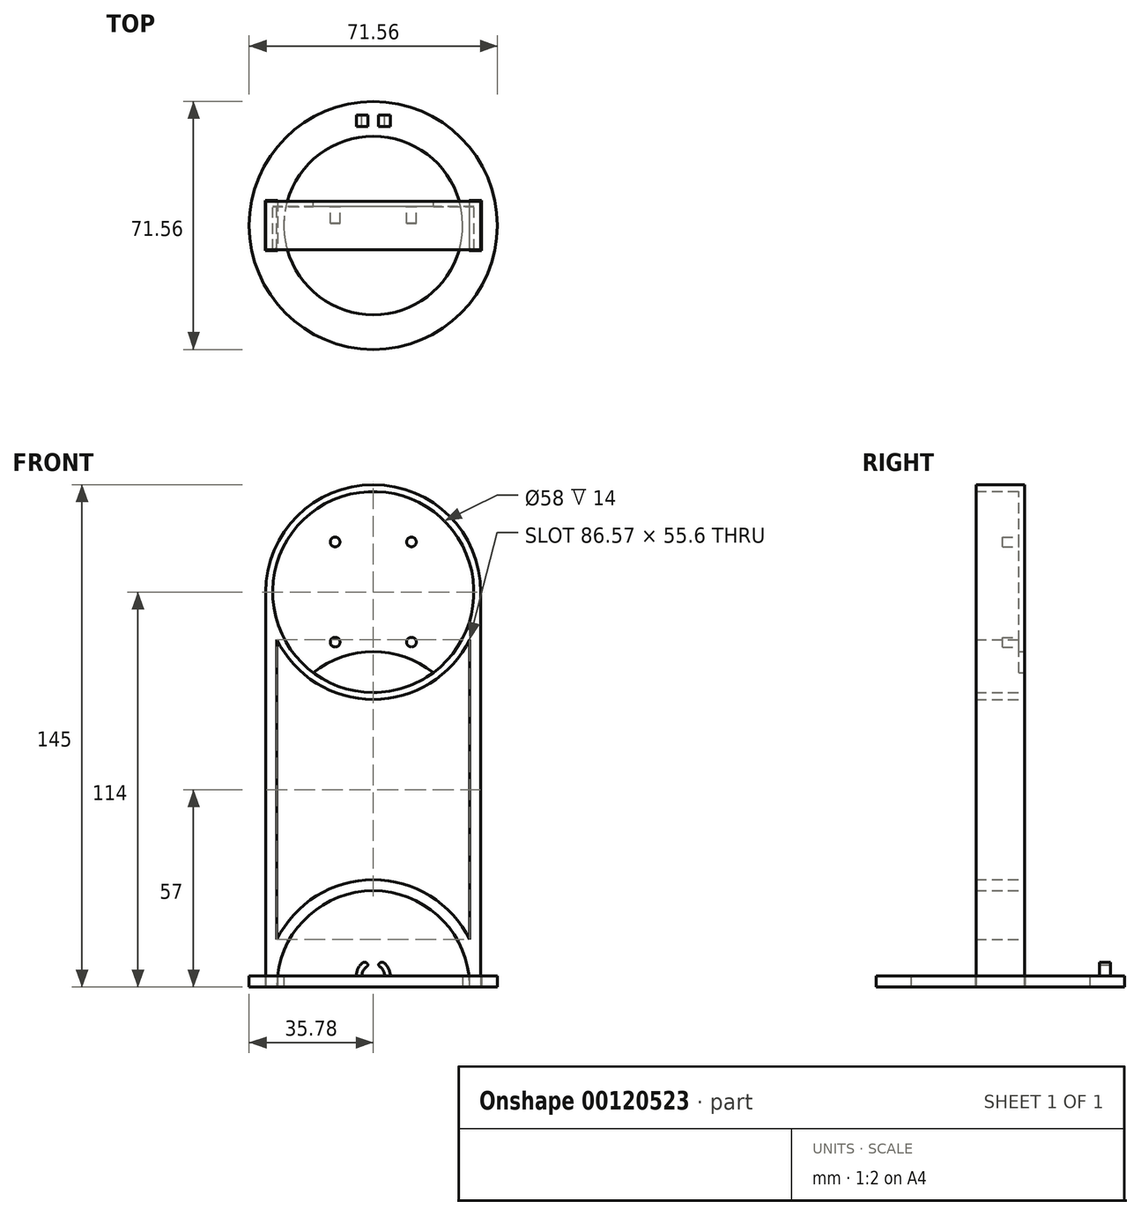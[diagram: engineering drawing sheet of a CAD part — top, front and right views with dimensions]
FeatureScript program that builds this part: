
annotation { "Feature Type Name" : "Feature", "Feature Type Description" : "" }
export const myFeature = defineFeature(function(context is Context, id is Id, definition is map)
    precondition{}
    {
        {
            var Q0;
            Q0=qCreatedBy(makeId("Front.planeOp"),FACE);
            var sketch = newSketch(context, id + "F0", { "sketchPlane" : qUnion([Q0])});
            skCircle(sketch, "E0", {"center": v(0, 0) * mm, "radius": 29 * mm});
            skArc(sketch, "E1", {"start": v(31, 0) * mm, "mid": v(0, 31) * mm, "end": v(-31, 0) * mm});
            skCircle(sketch, "E2", {"center": v(-11, 14.45) * mm, "radius": 1.4 * mm});
            skCircle(sketch, "E3.0.1.0", {"center": v(-11, -14.45) * mm, "radius": 1.4 * mm});
            skCircle(sketch, "E3.1.0.0", {"center": v(11, 14.45) * mm, "radius": 1.4 * mm});
            skCircle(sketch, "E3.1.1.0", {"center": v(11, -14.45) * mm, "radius": 1.4 * mm});
            skLineSegment(sketch, "E3.direction1", {"start": v(-11, 14.45) * mm, "end": v(11, 14.45) * mm, "construction": true});
            skLineSegment(sketch, "E3.direction2", {"start": v(-11, 14.45) * mm, "end": v(-11, -14.45) * mm, "construction": true});
            skLineSegment(sketch, "E4.top", {"start": v(-31, -114) * mm, "end": v(-27.8, -114) * mm});
            skLineSegment(sketch, "E4.left", {"start": v(-31, 0) * mm, "end": v(-31, -114) * mm});
            skLineSegment(sketch, "E4.right", {"start": v(-27.8, -13.72) * mm, "end": v(-27.8, -114) * mm});
            skLineSegment(sketch, "E5.MirrorCS", {"start": v(27.8, -13.72) * mm, "end": v(27.8, -114) * mm});
            skLineSegment(sketch, "E6.MirrorCS", {"start": v(31, -114) * mm, "end": v(27.8, -114) * mm});
            skLineSegment(sketch, "E7.MirrorCS", {"start": v(31, 0) * mm, "end": v(31, -114) * mm});
            skArc(sketch, "E8", {"start": v(27.8, -114) * mm, "mid": v(0, -86.2) * mm, "end": v(-27.8, -114) * mm});
            skArc(sketch, "E9.0", {"start": v(27.8, -100.28) * mm, "mid": v(0, -83) * mm, "end": v(-27.8, -100.28) * mm});
            skPoint(sketch, "E10.orphan", {"position": v(-27.8, 0) * mm});
            skPoint(sketch, "E11.orphan", {"position": v(27.8, 0) * mm});
            skArc(sketch, "E12.trimOffspring", {"start": v(-27.8, -13.72) * mm, "mid": v(0, -31) * mm, "end": v(27.8, -13.72) * mm});
            skCircle(sketch, "E13", {"center": v(0, -45) * mm, "radius": 27.8 * mm});
            skSolve(sketch);
        }
        {
            var Q0;
            Q0=makeQuery(id+"F0.imprint","IMPRINT",FACE,{"disambiguationData":[TD([[makeQuery(id+"F0.imprint","IMPRINT",EDGE,{"derivedFrom":sQuery(id+"F0.wireOp",EDGE,"E0")}),-1.0]])]});
            var Q1;
            {var subQ0=sQuery(id+"F0.wireOp",EDGE,"E8");Q1=makeQuery(id+"F0.imprint","IMPRINT",FACE,{"disambiguationData":[TD([[makeQuery(id+"F0.imprint","IMPRINT",EDGE,{"derivedFrom":subQ0}),-1.0]])]});}
            var Q2;
            Q2=makeQuery(id+"F0.imprint","IMPRINT",FACE,{"disambiguationData":[TD([[makeQuery(id+"F0.imprint","IMPRINT",EDGE,{"derivedFrom":sQuery(id+"F0.wireOp",EDGE,"E1")}),1.0]])]});
            extrude(context, id + "F1", {"entities" : qUnion([Q0, Q1, Q2]), "depth" : 14 * mm});
        }
        {
            var Q0;
            Q0=makeQuery(id+"F0.imprint","IMPRINT",FACE,{"disambiguationData":[TD([[makeQuery(id+"F0.imprint","IMPRINT",EDGE,{"derivedFrom":sQuery(id+"F0.wireOp",EDGE,"E2")}),-1.0]])]});
            extrude(context, id + "F2", {"entities" : qUnion([Q0]), "operationType" : NewBodyOperationType.ADD, "depth" : 1.6 * mm});
        }
        {
            var Q0;
            Q0=makeQuery(id+"F0.imprint","IMPRINT",FACE,{"disambiguationData":[TD([[makeQuery(id+"F0.imprint","IMPRINT",EDGE,{"derivedFrom":sQuery(id+"F0.wireOp",EDGE,"E3.1.1.0")}),1.0]])]});
            var Q1;
            Q1=makeQuery(id+"F0.imprint","IMPRINT",FACE,{"disambiguationData":[TD([[makeQuery(id+"F0.imprint","IMPRINT",EDGE,{"derivedFrom":sQuery(id+"F0.wireOp",EDGE,"E3.0.1.0")}),1.0]])]});
            var Q2;
            Q2=makeQuery(id+"F0.imprint","IMPRINT",FACE,{"disambiguationData":[TD([[makeQuery(id+"F0.imprint","IMPRINT",EDGE,{"derivedFrom":sQuery(id+"F0.wireOp",EDGE,"E2")}),1.0]])]});
            var Q3;
            Q3=makeQuery(id+"F0.imprint","IMPRINT",FACE,{"disambiguationData":[TD([[makeQuery(id+"F0.imprint","IMPRINT",EDGE,{"derivedFrom":sQuery(id+"F0.wireOp",EDGE,"E3.1.0.0")}),1.0]])]});
            extrude(context, id + "F3", {"entities" : qUnion([Q0, Q1, Q2, Q3]), "operationType" : NewBodyOperationType.ADD, "depth" : (4.8 + 1.6) * mm});
        }
        {
            var Q0;
            Q0=makeQuery(id+"F1.opExtrude","SWEPT_FACE",FACE,{"disambiguationData":[OSD([sQuery(id+"F0.wireOp",EDGE,"E6.MirrorCS")])]});
            var sketch = newSketch(context, id + "F4", { "sketchPlane" : qUnion([Q0])});
            skCircle(sketch, "E14", {"center": v(0, 7) * mm, "radius": 35.78 * mm});
            skLineSegment(sketch, "E15", {"start": v(0, 0) * mm, "end": v(0, 14) * mm, "construction": true});
            skCircle(sketch, "E16.0", {"center": v(0, 7) * mm, "radius": 25.78 * mm});
            skLineSegment(sketch, "E17", {"start": v(0, -18.78) * mm, "end": v(0, -28.78) * mm, "construction": true});
            skPoint(sketch, "E18", {"position": v(0, -23.78) * mm});
            skLineSegment(sketch, "E19", {"start": v(18.24, -23.78) * mm, "end": v(-18.24, -23.78) * mm, "construction": true});
            skLineSegment(sketch, "E20.bottom", {"start": v(-31, 0) * mm, "end": v(-27.8, 0) * mm, "construction": true});
            skLineSegment(sketch, "E20.top", {"start": v(-31, 14) * mm, "end": v(-27.8, 14) * mm, "construction": true});
            skLineSegment(sketch, "E20.left", {"start": v(-31, 0) * mm, "end": v(-31, 14) * mm, "construction": true});
            skLineSegment(sketch, "E20.right", {"start": v(-27.8, 0) * mm, "end": v(-27.8, 14) * mm, "construction": true});
            skLineSegment(sketch, "E21.bottom", {"start": v(27.8, 14) * mm, "end": v(31, 14) * mm, "construction": true});
            skLineSegment(sketch, "E21.top", {"start": v(27.8, 0) * mm, "end": v(31, 0) * mm, "construction": true});
            skLineSegment(sketch, "E21.left", {"start": v(27.8, 14) * mm, "end": v(27.8, 0) * mm, "construction": true});
            skLineSegment(sketch, "E21.right", {"start": v(31, 14) * mm, "end": v(31, 0) * mm, "construction": true});
            skLineSegment(sketch, "E22.0", {"start": v(-31.2, -0.2) * mm, "end": v(-31.2, 14.2) * mm});
            skLineSegment(sketch, "E22.1", {"start": v(-31.2, -0.2) * mm, "end": v(-27.6, -0.2) * mm});
            skLineSegment(sketch, "E22.2", {"start": v(-27.6, -0.2) * mm, "end": v(-27.6, 14.2) * mm});
            skLineSegment(sketch, "E22.3", {"start": v(-31.2, 14.2) * mm, "end": v(-27.6, 14.2) * mm});
            skLineSegment(sketch, "E23.MirrorCS", {"start": v(27.6, -0.2) * mm, "end": v(27.6, 14.2) * mm});
            skLineSegment(sketch, "E24.MirrorCS", {"start": v(31.2, 14.2) * mm, "end": v(27.6, 14.2) * mm});
            skLineSegment(sketch, "E25.MirrorCS", {"start": v(31.2, -0.2) * mm, "end": v(31.2, 14.2) * mm});
            skLineSegment(sketch, "E26.MirrorCS", {"start": v(31.2, -0.2) * mm, "end": v(27.6, -0.2) * mm});
            skSolve(sketch);
        }
        {
            var Q0;
            Q0=makeQuery(id+"F4.imprint","IMPRINT",FACE,{"disambiguationData":[TD([[makeQuery(id+"F4.imprint","IMPRINT",EDGE,{"derivedFrom":sQuery(id+"F4.wireOp",EDGE,"E14")}),1.0]])]});
            extrude(context, id + "F5", {"entities" : qUnion([Q0]), "oppositeDirection" : true, "depth" : 3.2 * mm});
        }
        {
            var Q0;
            Q0=qCreatedBy(makeId("Front.planeOp"),FACE);
            cPlane(context, id + "F6", {"entities" : qUnion([Q0]), "cplaneType" : CPlaneType.OFFSET, "offset" : 23.2 * mm, "oppositeDirection" : true, "width" : 150 * mm, "height" : 150 * mm});
        }
        {
            var Q0;
            Q0=qCreatedBy(id+"F6.planeOp",FACE);
            var sketch = newSketch(context, id + "F7", { "sketchPlane" : qUnion([Q0])});
            skArc(sketch, "E27", {"start": v(3.3, -110.8) * mm, "mid": v(2.81, -109.08) * mm, "end": v(1.5, -107.86) * mm});
            skLineSegment(sketch, "E28", {"start": v(-3.3, -110.8) * mm, "end": v(3.3, -110.8) * mm});
            skArc(sketch, "E29.0", {"start": v(4.9, -110.8) * mm, "mid": v(3.96, -107.91) * mm, "end": v(1.5, -106.14) * mm});
            skLineSegment(sketch, "E30.bottom", {"start": v(-1.5, -110.8) * mm, "end": v(1.5, -110.8) * mm});
            skLineSegment(sketch, "E30.left", {"start": v(-1.5, -107.86) * mm, "end": v(-1.5, -106.14) * mm});
            skLineSegment(sketch, "E30.right", {"start": v(1.5, -107.86) * mm, "end": v(1.5, -106.14) * mm});
            skArc(sketch, "E31.trimOffspring", {"start": v(-1.5, -107.86) * mm, "mid": v(-2.81, -109.08) * mm, "end": v(-3.3, -110.8) * mm});
            skArc(sketch, "E32.trimOffspring", {"start": v(-1.5, -106.14) * mm, "mid": v(-3.96, -107.91) * mm, "end": v(-4.9, -110.8) * mm});
            skLineSegment(sketch, "E33", {"start": v(3.3, -110.8) * mm, "end": v(4.9, -110.8) * mm});
            skLineSegment(sketch, "E34", {"start": v(-3.3, -110.8) * mm, "end": v(-4.9, -110.8) * mm});
            skSolve(sketch);
        }
        {
            var Q0;
            Q0=makeQuery(id+"F7.imprint","IMPRINT",FACE,{"disambiguationData":[TD([[makeQuery(id+"F7.imprint","IMPRINT",EDGE,{"derivedFrom":sQuery(id+"F7.wireOp",EDGE,"E27")}),-1.0]])]});
            var Q1;
            Q1=makeQuery(id+"F7.imprint","IMPRINT",FACE,{"disambiguationData":[TD([[makeQuery(id+"F7.imprint","IMPRINT",EDGE,{"derivedFrom":sQuery(id+"F7.wireOp",EDGE,"E30.left")}),1.0]])]});
            extrude(context, id + "F8", {"entities" : qUnion([Q0, Q1]), "operationType" : NewBodyOperationType.ADD, "depth" : 3.2 * mm, "symmetric" : true});
        }
        {
            var Q0;
            Q0=makeQuery(id+"F8.opExtrude","SWEPT_EDGE",EDGE,{"disambiguationData":[OSD([sQuery(id+"F7.wireOp",EDGE,"E27"),sQuery(id+"F7.wireOp",EDGE,"E30.right")])]});
            var Q1;
            Q1=makeQuery(id+"F8.opExtrude","SWEPT_EDGE",EDGE,{"disambiguationData":[OSD([sQuery(id+"F7.wireOp",EDGE,"E29.0"),sQuery(id+"F7.wireOp",EDGE,"E30.right")])]});
            var Q2;
            Q2=makeQuery(id+"F8.opExtrude","SWEPT_EDGE",EDGE,{"disambiguationData":[OSD([sQuery(id+"F7.wireOp",EDGE,"E30.left"),sQuery(id+"F7.wireOp",EDGE,"E31.trimOffspring")])]});
            var Q3;
            Q3=makeQuery(id+"F8.opExtrude","SWEPT_EDGE",EDGE,{"disambiguationData":[OSD([sQuery(id+"F7.wireOp",EDGE,"E30.left"),sQuery(id+"F7.wireOp",EDGE,"E32.trimOffspring")])]});
            var Q4;
            Q4=makeQuery(id+"F8.opExtrude","SWEPT_EDGE",EDGE,{"disambiguationData":[OSD([sQuery(id+"F7.wireOp",EDGE,"E29.0"),sQuery(id+"F7.wireOp",EDGE,"E33")])]});
            var Q5;
            Q5=makeQuery(id+"F8.opExtrude","SWEPT_EDGE",EDGE,{"disambiguationData":[OSD([sQuery(id+"F7.wireOp",EDGE,"E32.trimOffspring"),sQuery(id+"F7.wireOp",EDGE,"E34")])]});
            var Q6;
            Q6=makeQuery(id+"F8.opExtrude","SWEPT_EDGE",EDGE,{"disambiguationData":[OSD([sQuery(id+"F7.wireOp",EDGE,"E27"),sQuery(id+"F7.wireOp",EDGE,"E33")])]});
            var Q7;
            Q7=makeQuery(id+"F8.opExtrude","SWEPT_EDGE",EDGE,{"disambiguationData":[OSD([sQuery(id+"F7.wireOp",EDGE,"E31.trimOffspring"),sQuery(id+"F7.wireOp",EDGE,"E34")])]});
            fillet(context, id + "F9", {"entities" : qUnion([Q0, Q1, Q2, Q3, Q4, Q5, Q6, Q7]), "radius" : 1 * mm, "tangentPropagation" : true, "allowEdgeOverflow" : false});
        }
        {
            var Q0;
            Q0=makeQuery(id+"F1.opExtrude","SWEPT_EDGE",EDGE,{"disambiguationData":[OSD([sQuery(id+"F0.wireOp",EDGE,"E5.MirrorCS"),sQuery(id+"F0.wireOp",EDGE,"E6.MirrorCS"),sQuery(id+"F0.wireOp",EDGE,"E8")])]});
            var Q1;
            Q1=makeQuery(id+"F1.opExtrude","SWEPT_EDGE",EDGE,{"disambiguationData":[OSD([sQuery(id+"F0.wireOp",EDGE,"E6.MirrorCS"),sQuery(id+"F0.wireOp",EDGE,"E7.MirrorCS")])]});
            var Q2;
            Q2=makeQuery(id+"F1.opExtrude","CAP_EDGE",EDGE,{"disambiguationData":[OSD([sQuery(id+"F0.wireOp",EDGE,"E6.MirrorCS")])],"isStart":false});
            var Q3;
            Q3=makeQuery(id+"F1.opExtrude","CAP_EDGE",EDGE,{"disambiguationData":[OSD([sQuery(id+"F0.wireOp",EDGE,"E6.MirrorCS")])],"isStart":true});
            var Q4;
            Q4=makeQuery(id+"F1.opExtrude","CAP_EDGE",EDGE,{"disambiguationData":[OSD([sQuery(id+"F0.wireOp",EDGE,"E4.top")])],"isStart":true});
            var Q5;
            Q5=makeQuery(id+"F1.opExtrude","SWEPT_EDGE",EDGE,{"disambiguationData":[OSD([sQuery(id+"F0.wireOp",EDGE,"E4.top"),sQuery(id+"F0.wireOp",EDGE,"E4.left")])]});
            var Q6;
            Q6=makeQuery(id+"F1.opExtrude","SWEPT_EDGE",EDGE,{"disambiguationData":[OSD([sQuery(id+"F0.wireOp",EDGE,"E4.top"),sQuery(id+"F0.wireOp",EDGE,"E4.right"),sQuery(id+"F0.wireOp",EDGE,"E8")])]});
            var Q7;
            Q7=makeQuery(id+"F1.opExtrude","CAP_EDGE",EDGE,{"disambiguationData":[OSD([sQuery(id+"F0.wireOp",EDGE,"E4.top")])],"isStart":false});
            fillet(context, id + "F10", {"entities" : qUnion([Q0, Q1, Q2, Q3, Q4, Q5, Q6, Q7]), "radius" : 0.4 * mm, "tangentPropagation" : true, "allowEdgeOverflow" : false});
        }
    });
